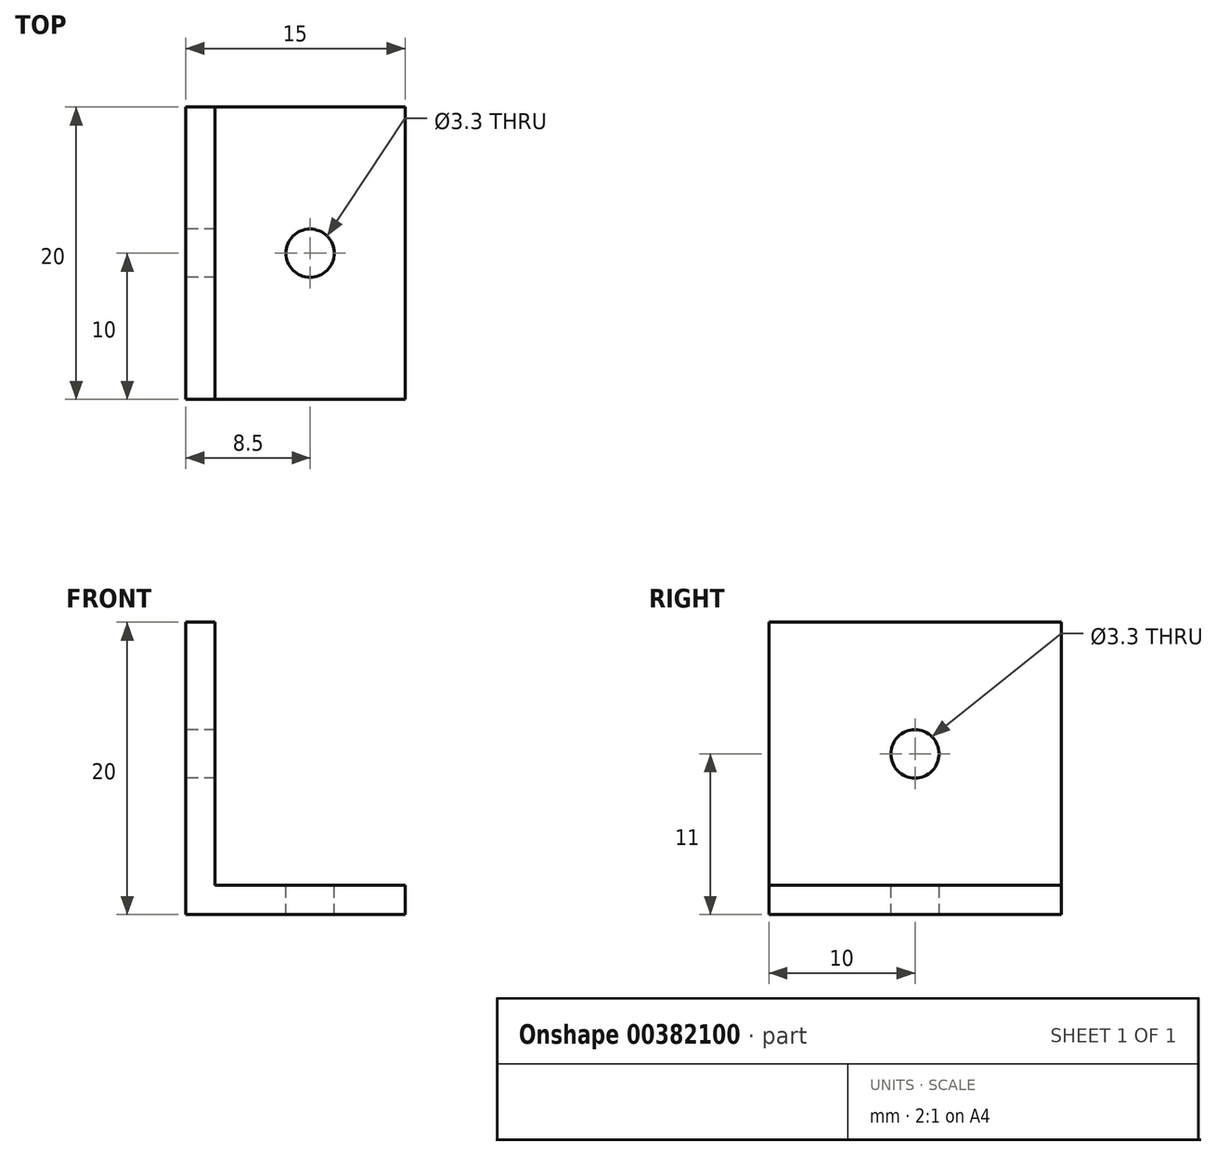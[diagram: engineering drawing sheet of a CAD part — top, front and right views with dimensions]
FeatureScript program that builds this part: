
annotation { "Feature Type Name" : "Feature", "Feature Type Description" : "" }
export const myFeature = defineFeature(function(context is Context, id is Id, definition is map)
    precondition{}
    {
        {
            var Q0;
            Q0=qCreatedBy(makeId("Front.planeOp"),FACE);
            var sketch = newSketch(context, id + "F0", { "sketchPlane" : qUnion([Q0])});
            skLineSegment(sketch, "E0", {"start": v(0, 0) * mm, "end": v(0, 20) * mm});
            skLineSegment(sketch, "E1", {"start": v(0, 20) * mm, "end": v(2, 20) * mm});
            skLineSegment(sketch, "E2", {"start": v(2, 20) * mm, "end": v(2, 2) * mm});
            skLineSegment(sketch, "E3", {"start": v(2, 2) * mm, "end": v(15, 2) * mm});
            skLineSegment(sketch, "E4", {"start": v(15, 2) * mm, "end": v(15, 0) * mm});
            skLineSegment(sketch, "E5", {"start": v(15, 0) * mm, "end": v(0, 0) * mm});
            skSolve(sketch);
        }
        {
            var Q0;
            Q0=makeQuery(id+"F0.imprint","IMPRINT",FACE,{"disambiguationData":[TD([[makeQuery(id+"F0.imprint","IMPRINT",EDGE,{"derivedFrom":sQuery(id+"F0.wireOp",EDGE,"E0")}),-1.0]])]});
            extrude(context, id + "F1", {"entities" : qUnion([Q0]), "endBound" : BoundingType.SYMMETRIC, "depth" : 20 * mm});
        }
        {
            var Q0;
            Q0=makeQuery(id+"F1.opExtrude","SWEPT_FACE",FACE,{"disambiguationData":[OSD([sQuery(id+"F0.wireOp",EDGE,"E0")])]});
            var sketch = newSketch(context, id + "F2", { "sketchPlane" : qUnion([Q0])});
            skLineSegment(sketch, "E6.0", {"start": v(10, 2) * mm, "end": v(-10, 2) * mm});
            skLineSegment(sketch, "E7.0", {"start": v(10, 20) * mm, "end": v(-10, 20) * mm});
            skLineSegment(sketch, "E8", {"start": v(0, 20) * mm, "end": v(0, 2) * mm, "construction": true});
            skPoint(sketch, "E9", {"position": v(0, 11) * mm});
            skSolve(sketch);
        }
        {
            var Q0;
            Q0=makeQuery(id+"F1.opExtrude","SWEPT_FACE",FACE,{"disambiguationData":[OSD([sQuery(id+"F0.wireOp",EDGE,"E3")])]});
            var sketch = newSketch(context, id + "F3", { "sketchPlane" : qUnion([Q0])});
            skLineSegment(sketch, "E10", {"start": v(2, 0) * mm, "end": v(15, 0) * mm, "construction": true});
            skPoint(sketch, "E11", {"position": v(8.5, 0) * mm});
            skSolve(sketch);
        }
        {
            var Q0;
            Q0=sQuery(id+"F2.wireOp",VERTEX,"E9");
            var Q1;
            Q1=sQuery(id+"F3.wireOp",VERTEX,"E11");
            var Q2;
            Q2=makeQuery(id+"F1.opExtrude","SWEPT_BODY",BODY,{"disambiguationData":[OSD([sQuery(id+"F0.wireOp",EDGE,"E0"),sQuery(id+"F0.wireOp",EDGE,"E1"),sQuery(id+"F0.wireOp",EDGE,"E2"),sQuery(id+"F0.wireOp",EDGE,"E3"),sQuery(id+"F0.wireOp",EDGE,"E4"),sQuery(id+"F0.wireOp",EDGE,"E5")])]});
            var Q3;
            Q3=makeQuery(id+"F1.opExtrude","SWEPT_BODY",BODY,{"disambiguationData":[OSD([sQuery(id+"F0.wireOp",EDGE,"E0"),sQuery(id+"F0.wireOp",EDGE,"E1"),sQuery(id+"F0.wireOp",EDGE,"E2"),sQuery(id+"F0.wireOp",EDGE,"E3"),sQuery(id+"F0.wireOp",EDGE,"E4"),sQuery(id+"F0.wireOp",EDGE,"E5")])]});
            hole(context, id + "F4", {"style" : HoleStyle.SIMPLE, "endStyle" : HoleEndStyle.THROUGH, "standardTappedOrClearance" : lookupTablePath({ "standard" : "ISO", "fit" : "Normal", "size" : "M3", "type" : "Clearance" }), "standardBlindInLast" : lookupTablePath({ "fit" : "Standard", "standard" : "ISO", "size" : "M3", "type" : "Clearance" }), "holeDiameter" : 3.3 * mm, "isTappedThrough" : true, "tappedDepth" : 3 * mm, "tapClearance" : 3, "locations" : qUnion([Q0, Q1]), "scope" : qUnion([Q2, Q3])});
        }
    });
